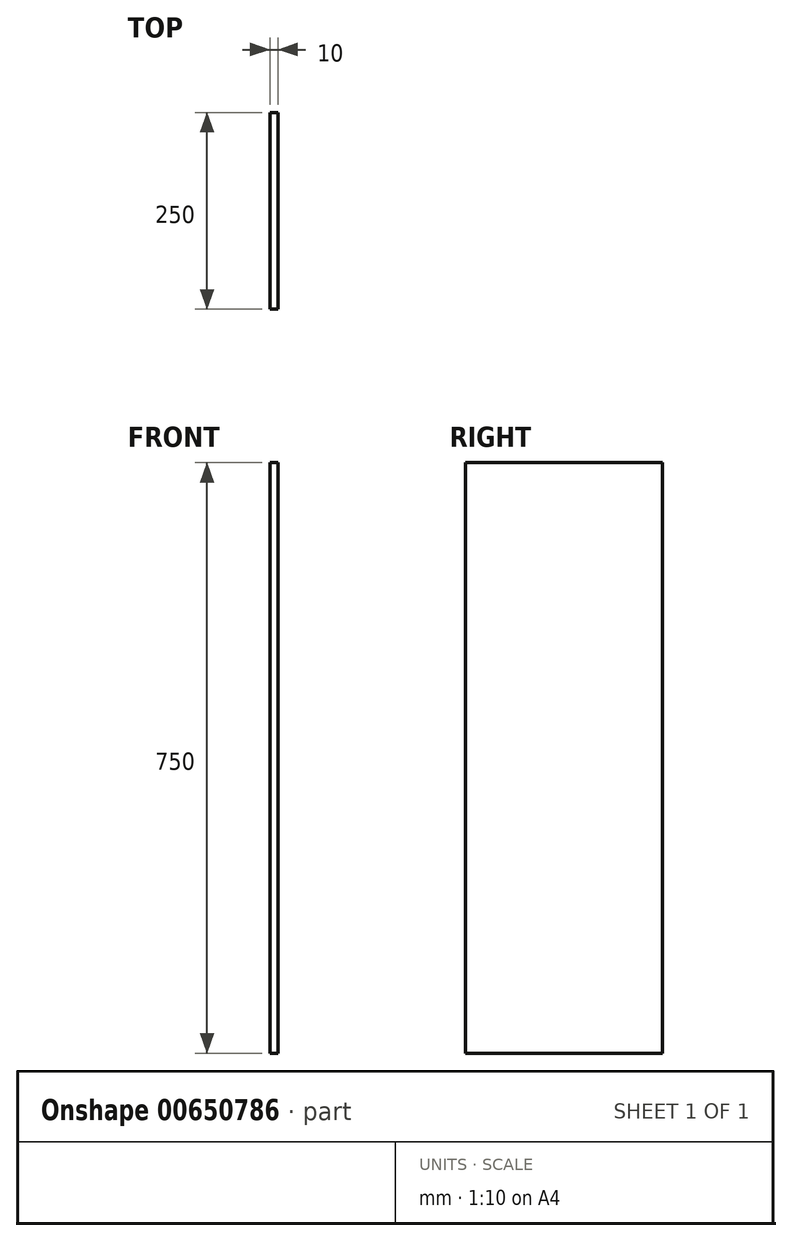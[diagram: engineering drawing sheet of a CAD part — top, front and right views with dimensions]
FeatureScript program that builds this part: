
annotation { "Feature Type Name" : "Feature", "Feature Type Description" : "" }
export const myFeature = defineFeature(function(context is Context, id is Id, definition is map)
    precondition{}
    {
        {
            var Q0;
            Q0=qCreatedBy(makeId("Right.planeOp"),FACE);
            var sketch = newSketch(context, id + "F0", { "sketchPlane" : qUnion([Q0])});
            skLineSegment(sketch, "E0.bottom", {"start": v(-138.22, 352.9) * mm, "end": v(111.78, 352.9) * mm});
            skLineSegment(sketch, "E0.top", {"start": v(-138.22, -397.1) * mm, "end": v(111.78, -397.1) * mm});
            skLineSegment(sketch, "E0.left", {"start": v(-138.22, 352.9) * mm, "end": v(-138.22, -397.1) * mm});
            skLineSegment(sketch, "E0.right", {"start": v(111.78, 352.9) * mm, "end": v(111.78, -397.1) * mm});
            skSolve(sketch);
        }
        {
            var Q0;
            Q0=makeQuery(id+"F0.imprint","IMPRINT",FACE,{"disambiguationData":[TD([[makeQuery(id+"F0.imprint","IMPRINT",EDGE,{"derivedFrom":sQuery(id+"F0.wireOp",EDGE,"E0.bottom")}),-1.0]])]});
            extrude(context, id + "F1", {"entities" : qUnion([Q0]), "depth" : 10 * mm, "offsetDistance" : 25 * mm});
        }
    });
